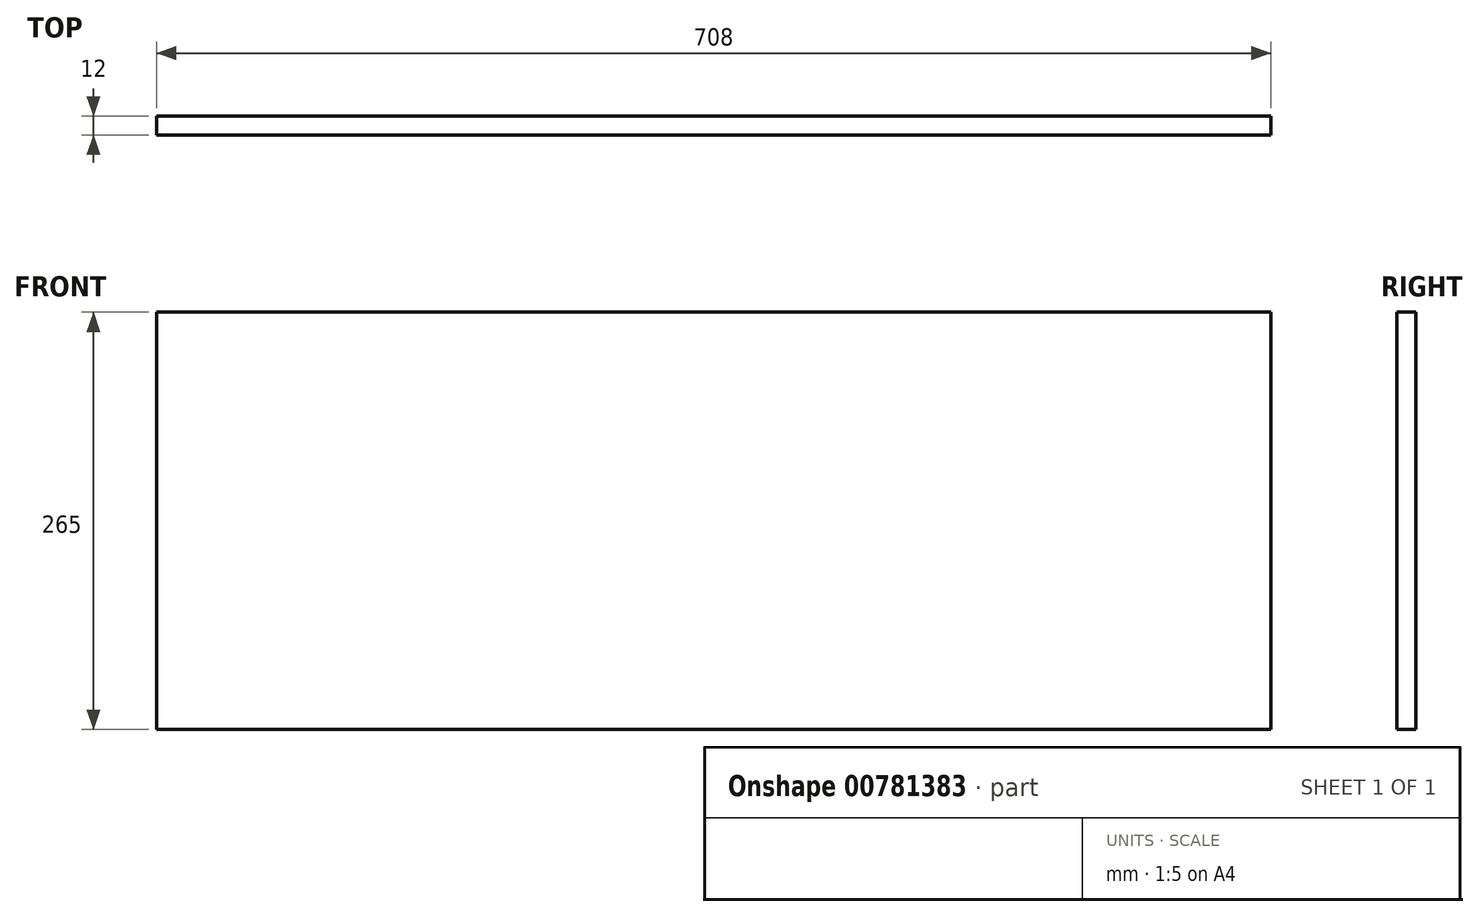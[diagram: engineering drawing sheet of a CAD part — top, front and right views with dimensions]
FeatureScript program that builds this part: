
annotation { "Feature Type Name" : "Feature", "Feature Type Description" : "" }
export const myFeature = defineFeature(function(context is Context, id is Id, definition is map)
    precondition{}
    {
        {
            var Q0;
            Q0=qCreatedBy(makeId("Front.planeOp"),FACE);
            var sketch = newSketch(context, id + "F0", { "sketchPlane" : qUnion([Q0])});
            skLineSegment(sketch, "E0.bottom", {"start": v(372.11, -132.5) * mm, "end": v(-335.89, -132.5) * mm});
            skLineSegment(sketch, "E0.top", {"start": v(372.11, 132.5) * mm, "end": v(-335.89, 132.5) * mm});
            skLineSegment(sketch, "E0.left", {"start": v(372.11, -132.5) * mm, "end": v(372.11, 132.5) * mm});
            skLineSegment(sketch, "E0.right", {"start": v(-335.89, -132.5) * mm, "end": v(-335.89, 132.5) * mm});
            skPoint(sketch, "E0.middle", {"position": v(18.11, 0) * mm});
            skSolve(sketch);
        }
        {
            var Q0;
            Q0 = qSketchRegion(id + "F0", true);
            extrude(context, id + "F1", {"entities" : qUnion([Q0]), "depth" : 12 * mm, "offsetDistance" : 25 * mm});
        }
    });
